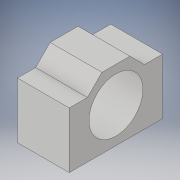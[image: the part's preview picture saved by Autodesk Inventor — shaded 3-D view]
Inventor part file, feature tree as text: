
AUTODESK INVENTOR PART (.ipt)
format: ipt  version: 2019 (Build 230136000, 136)  size: 105,984 bytes
history: native  units: in
note: dims shown in document units (in); Inventor stores cm internally (conversion verified against a paired STEP export)
features: extrude x1, sketch x1
ambient origin geometry x8: Origin, YZ Plane, XZ Plane, XY Plane, X Axis, Y Axis, Z Axis, Center Point
bodies: Solid1 (feature_tree)
feature tree (2):
  extrude  "Extrusion1"  Depth=2.126in
  sketch  "Sketch1"  dims[d0=1.7717in d1=2.126in d2=1.0827in d4=0.5315in d5=2.6772in d6=2.0472in d7=1.3386in d8=1.9685in d9=0.0in]
